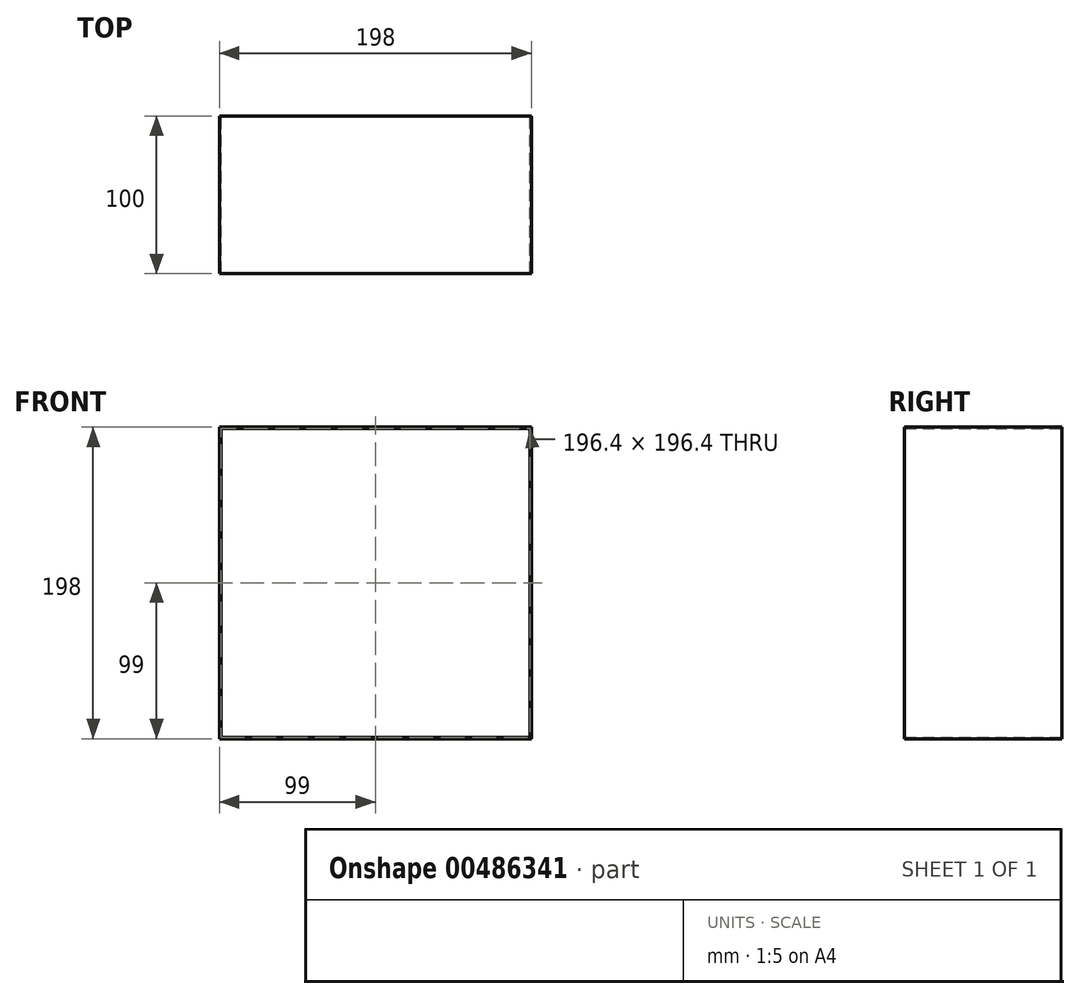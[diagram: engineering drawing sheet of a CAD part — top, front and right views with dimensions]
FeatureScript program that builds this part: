
annotation { "Feature Type Name" : "Feature", "Feature Type Description" : "" }
export const myFeature = defineFeature(function(context is Context, id is Id, definition is map)
    precondition{}
    {
        {
            var Q0;
            Q0=qCreatedBy(makeId("Front.planeOp"),FACE);
            var sketch = newSketch(context, id + "F0", { "sketchPlane" : qUnion([Q0])});
            skLineSegment(sketch, "E0.bottom", {"start": v(0, 0) * mm, "end": v(198, 0) * mm});
            skLineSegment(sketch, "E0.top", {"start": v(0, 198) * mm, "end": v(198, 198) * mm});
            skLineSegment(sketch, "E0.left", {"start": v(0, 0) * mm, "end": v(0, 198) * mm});
            skLineSegment(sketch, "E0.right", {"start": v(198, 0) * mm, "end": v(198, 198) * mm});
            skLineSegment(sketch, "E1.0", {"start": v(0.8, 197.2) * mm, "end": v(197.2, 197.2) * mm});
            skLineSegment(sketch, "E1.1", {"start": v(0.8, 0.8) * mm, "end": v(0.8, 197.2) * mm});
            skLineSegment(sketch, "E1.2", {"start": v(0.8, 0.8) * mm, "end": v(197.2, 0.8) * mm});
            skLineSegment(sketch, "E1.3", {"start": v(197.2, 0.8) * mm, "end": v(197.2, 197.2) * mm});
            skSolve(sketch);
        }
        {
            var Q0;
            Q0 = qSketchRegion(id + "F0", true);
            extrude(context, id + "F1", {"entities" : qUnion([Q0]), "depth" : 100 * mm});
        }
    });
